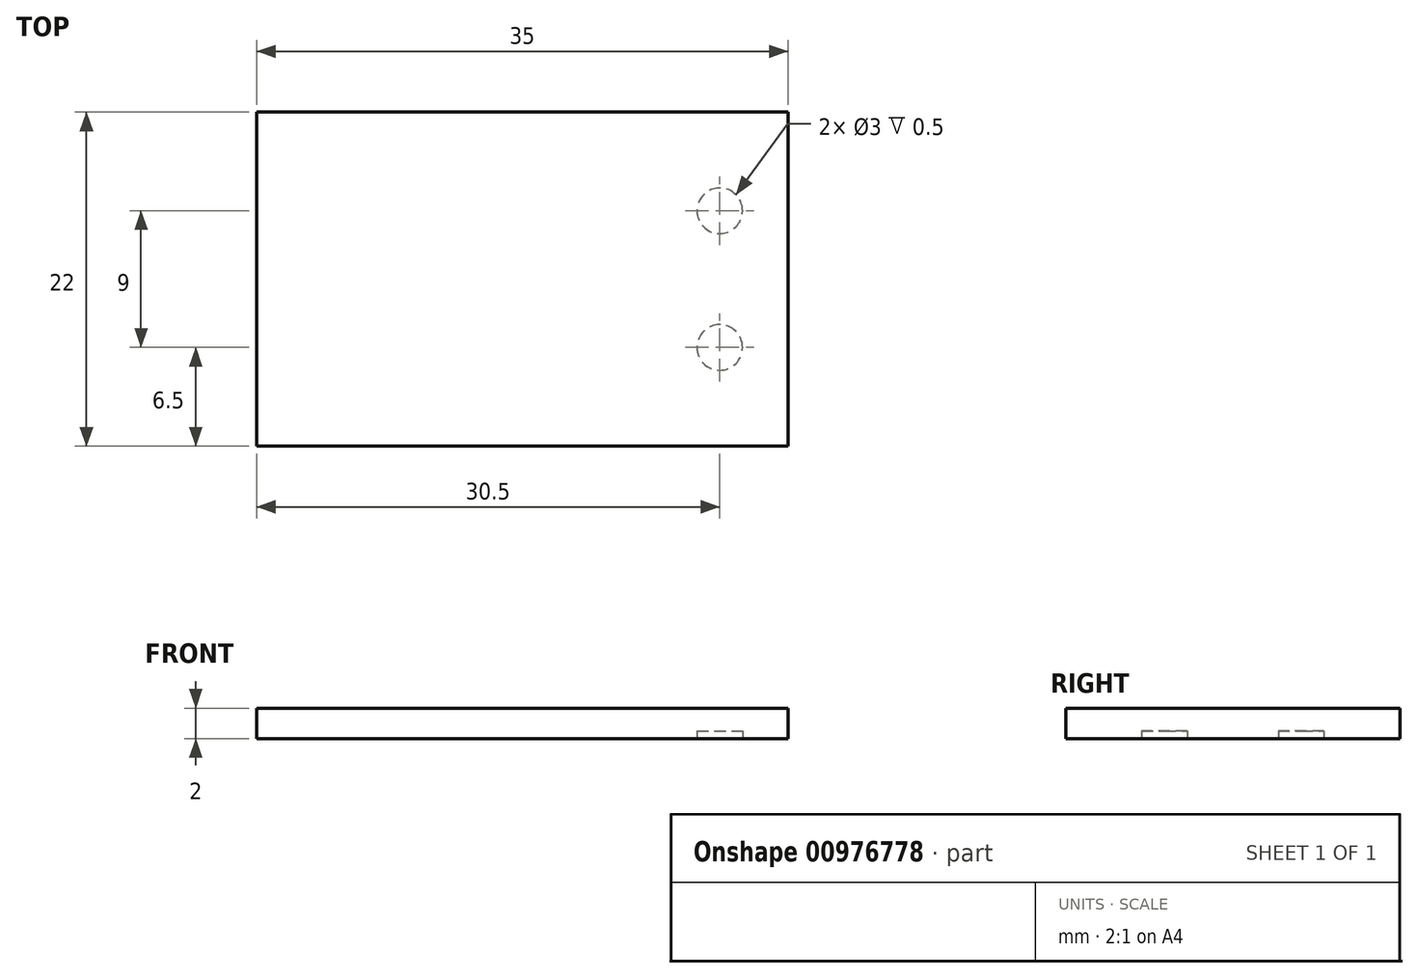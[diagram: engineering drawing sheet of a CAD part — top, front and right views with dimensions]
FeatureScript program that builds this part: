
annotation { "Feature Type Name" : "Feature", "Feature Type Description" : "" }
export const myFeature = defineFeature(function(context is Context, id is Id, definition is map)
    precondition{}
    {
        {
            var Q0;
            Q0=qCreatedBy(makeId("Top.planeOp"),FACE);
            var sketch = newSketch(context, id + "F0", { "sketchPlane" : qUnion([Q0])});
            skLineSegment(sketch, "E0.bottom", {"start": v(17.5, -11) * mm, "end": v(-17.5, -11) * mm});
            skLineSegment(sketch, "E0.top", {"start": v(17.5, 11) * mm, "end": v(-17.5, 11) * mm});
            skLineSegment(sketch, "E0.left", {"start": v(17.5, -11) * mm, "end": v(17.5, 11) * mm});
            skLineSegment(sketch, "E0.right", {"start": v(-17.5, -11) * mm, "end": v(-17.5, 11) * mm});
            skPoint(sketch, "E0.middle", {"position": v(0, 0) * mm});
            skSolve(sketch);
        }
        {
            var Q0;
            Q0=makeQuery(id+"F0.imprint","IMPRINT",FACE,{"disambiguationData":[TD([[makeQuery(id+"F0.imprint","IMPRINT",EDGE,{"derivedFrom":sQuery(id+"F0.wireOp",EDGE,"E0.bottom")}),-1.0]])]});
            extrude(context, id + "F1", {"entities" : qUnion([Q0]), "depth" : 2 * mm, "offsetDistance" : 25 * mm});
        }
        {
            var Q0;
            Q0=makeQuery(id+"F1.opExtrude","CAP_FACE",FACE,{"disambiguationData":[OSD([sQuery(id+"F0.wireOp",EDGE,"E0.bottom"),sQuery(id+"F0.wireOp",EDGE,"E0.top"),sQuery(id+"F0.wireOp",EDGE,"E0.left"),sQuery(id+"F0.wireOp",EDGE,"E0.right")])],"isStart":true});
            var sketch = newSketch(context, id + "F2", { "sketchPlane" : qUnion([Q0])});
            skCircle(sketch, "E1", {"center": v(13, 4.5) * mm, "radius": 1.5 * mm});
            skCircle(sketch, "E2", {"center": v(13, -4.5) * mm, "radius": 1.5 * mm});
            skSolve(sketch);
        }
        {
            var Q0;
            Q0=makeQuery(id+"F2.imprint","IMPRINT",FACE,{"disambiguationData":[TD([[makeQuery(id+"F2.imprint","IMPRINT",EDGE,{"derivedFrom":sQuery(id+"F2.wireOp",EDGE,"E1")}),1.0]])]});
            var Q1;
            Q1=makeQuery(id+"F2.imprint","IMPRINT",FACE,{"disambiguationData":[TD([[makeQuery(id+"F2.imprint","IMPRINT",EDGE,{"derivedFrom":sQuery(id+"F2.wireOp",EDGE,"E2")}),1.0]])]});
            extrude(context, id + "F3", {"entities" : qUnion([Q0, Q1]), "operationType" : NewBodyOperationType.REMOVE, "oppositeDirection" : true, "depth" : .5 * mm, "offsetDistance" : 25 * mm});
        }
    });
